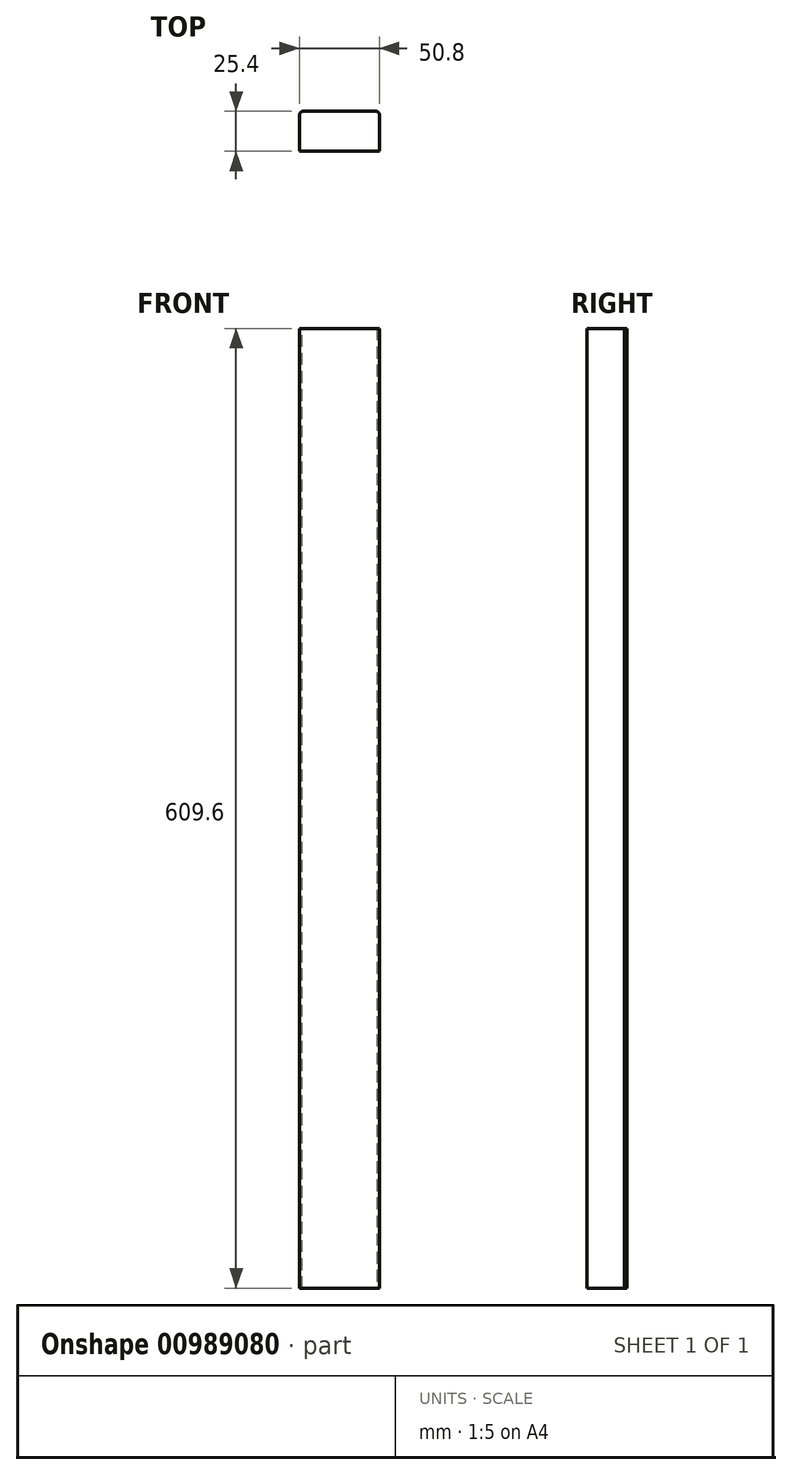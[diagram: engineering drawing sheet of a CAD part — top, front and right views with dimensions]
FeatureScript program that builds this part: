
annotation { "Feature Type Name" : "Feature", "Feature Type Description" : "" }
export const myFeature = defineFeature(function(context is Context, id is Id, definition is map)
    precondition{}
    {
        {
            var Q0;
            Q0=qCreatedBy(makeId("Top.planeOp"),FACE);
            var sketch = newSketch(context, id + "F0", { "sketchPlane" : qUnion([Q0])});
            skLineSegment(sketch, "E0.bottom", {"start": v(-25.4, 12.7) * mm, "end": v(25.4, 12.7) * mm});
            skLineSegment(sketch, "E0.top", {"start": v(-25.4, -12.7) * mm, "end": v(25.4, -12.7) * mm});
            skLineSegment(sketch, "E0.left", {"start": v(-25.4, 12.7) * mm, "end": v(-25.4, -12.7) * mm});
            skLineSegment(sketch, "E0.right", {"start": v(25.4, 12.7) * mm, "end": v(25.4, -12.7) * mm});
            skPoint(sketch, "E0.middle", {"position": v(0, 0) * mm});
            skSolve(sketch);
        }
        {
            var Q0;
            Q0 = qSketchRegion(id + "F0", true);
            extrude(context, id + "F1", {"entities" : qUnion([Q0]), "endBound" : BoundingType.SYMMETRIC, "depth" : 609.6 * mm, "offsetDistance" : 25.4 * mm});
        }
        {
            var Q0;
            Q0=makeQuery(id+"F1.opExtrude","SWEPT_EDGE",EDGE,{"disambiguationData":[OSD([sQuery(id+"F0.wireOp",EDGE,"E0.bottom"),sQuery(id+"F0.wireOp",EDGE,"E0.right")])]});
            var Q1;
            Q1=makeQuery(id+"F1.opExtrude","SWEPT_EDGE",EDGE,{"disambiguationData":[OSD([sQuery(id+"F0.wireOp",EDGE,"E0.bottom"),sQuery(id+"F0.wireOp",EDGE,"E0.left")])]});
            chamfer(context, id + "F2", {"entities" : qUnion([Q0, Q1]), "width" : 1.59 * mm, "tangentPropagation" : true});
        }
    });
